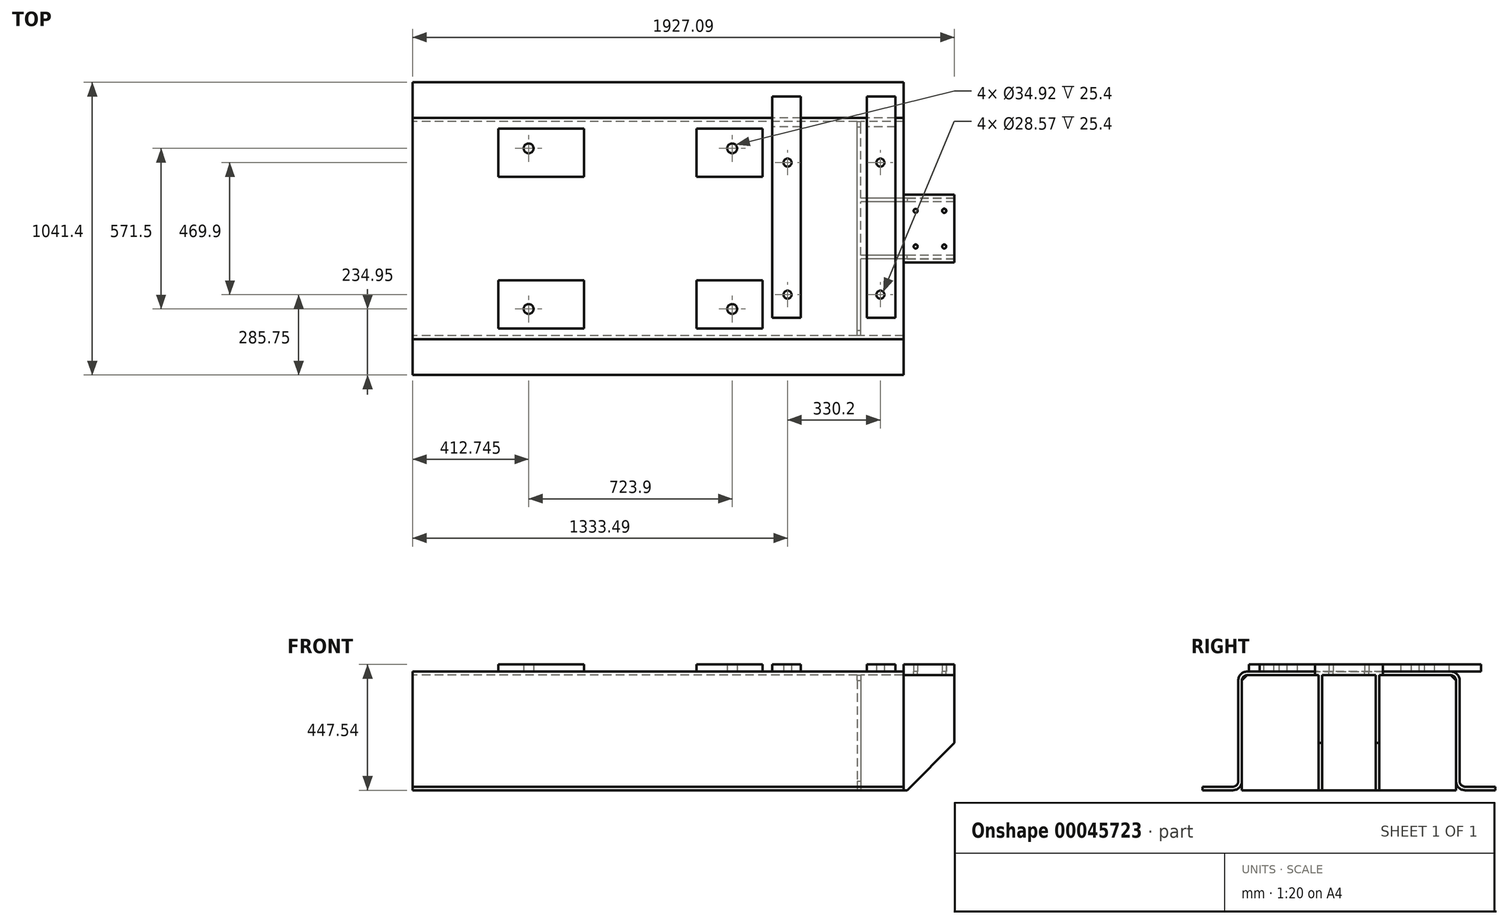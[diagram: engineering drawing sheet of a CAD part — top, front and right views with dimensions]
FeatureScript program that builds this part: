
annotation { "Feature Type Name" : "Feature", "Feature Type Description" : "" }
export const myFeature = defineFeature(function(context is Context, id is Id, definition is map)
    precondition{}
    {
        {
            var Q0;
            Q0=qCreatedBy(makeId("Right.planeOp"),FACE);
            var sketch = newSketch(context, id + "F0", { "sketchPlane" : qUnion([Q0])});
            skLineSegment(sketch, "E0.rect.bottom", {"start": v(-361.95, 211.07) * mm, "end": v(361.95, 211.07) * mm});
            skLineSegment(sketch, "E0.rect.top", {"start": v(-520.7, -211.07) * mm, "end": v(-412.75, -211.07) * mm});
            skLineSegment(sketch, "E0.rect.left", {"start": v(-393.7, 179.32) * mm, "end": v(-393.7, -179.32) * mm});
            skLineSegment(sketch, "E0.rect.right", {"start": v(393.7, 179.32) * mm, "end": v(393.7, -179.32) * mm});
            skPoint(sketch, "E0.rect.middle", {"position": v(0, 0) * mm});
            skLineSegment(sketch, "E1.0", {"start": v(-361.95, 198.37) * mm, "end": v(361.95, 198.37) * mm});
            skLineSegment(sketch, "E1.1", {"start": v(-381, 179.32) * mm, "end": v(-381, -179.32) * mm});
            skLineSegment(sketch, "E1.2", {"start": v(-520.7, -198.37) * mm, "end": v(-412.75, -198.37) * mm});
            skLineSegment(sketch, "E1.3", {"start": v(381, 179.32) * mm, "end": v(381, -179.32) * mm});
            skLineSegment(sketch, "E2.0", {"start": v(-520.7, -198.37) * mm, "end": v(-520.7, -211.07) * mm});
            skLineSegment(sketch, "E3", {"start": v(0, 0) * mm, "end": v(0, 407.59) * mm, "construction": true});
            skPoint(sketch, "E4.orphan", {"position": v(-393.7, -211.07) * mm});
            skLineSegment(sketch, "E5.MirrorCS", {"start": v(520.7, -198.37) * mm, "end": v(520.7, -211.07) * mm});
            skPoint(sketch, "E6.MirrorP", {"position": v(393.7, -211.07) * mm});
            skLineSegment(sketch, "E7.MirrorCS", {"start": v(520.7, -211.07) * mm, "end": v(412.75, -211.07) * mm});
            skLineSegment(sketch, "E8.MirrorCS", {"start": v(520.7, -198.37) * mm, "end": v(412.75, -198.37) * mm});
            skPoint(sketch, "E9.visualSharp", {"position": v(-393.7, -198.37) * mm});
            skArc(sketch, "E9.filletArc", {"start": v(-412.75, -198.37) * mm, "mid": v(-399.28, -192.8) * mm, "end": v(-393.7, -179.32) * mm});
            skPoint(sketch, "E10.visualSharp", {"position": v(-381, 198.37) * mm});
            skArc(sketch, "E10.filletArc", {"start": v(-361.95, 198.37) * mm, "mid": v(-375.42, 192.8) * mm, "end": v(-381, 179.32) * mm});
            skPoint(sketch, "E11.visualSharp", {"position": v(381, 198.37) * mm});
            skArc(sketch, "E11.filletArc", {"start": v(381, 179.32) * mm, "mid": v(375.42, 192.8) * mm, "end": v(361.95, 198.37) * mm});
            skPoint(sketch, "E12.visualSharp", {"position": v(393.7, -198.37) * mm});
            skArc(sketch, "E12.filletArc", {"start": v(393.7, -179.32) * mm, "mid": v(399.28, -192.8) * mm, "end": v(412.75, -198.37) * mm});
            skPoint(sketch, "E13.visualSharp", {"position": v(-381, -211.07) * mm});
            skArc(sketch, "E13.filletArc", {"start": v(-412.75, -211.07) * mm, "mid": v(-390.3, -201.77) * mm, "end": v(-381, -179.32) * mm});
            skPoint(sketch, "E14.visualSharp", {"position": v(-393.7, 211.07) * mm});
            skArc(sketch, "E14.filletArc", {"start": v(-361.95, 211.07) * mm, "mid": v(-384.4, 201.77) * mm, "end": v(-393.7, 179.32) * mm});
            skPoint(sketch, "E15.visualSharp", {"position": v(393.7, 211.07) * mm});
            skArc(sketch, "E15.filletArc", {"start": v(393.7, 179.32) * mm, "mid": v(384.4, 201.77) * mm, "end": v(361.95, 211.07) * mm});
            skPoint(sketch, "E16.visualSharp", {"position": v(381, -211.07) * mm});
            skArc(sketch, "E16.filletArc", {"start": v(381, -179.32) * mm, "mid": v(390.3, -201.77) * mm, "end": v(412.75, -211.07) * mm});
            skSolve(sketch);
        }
        {
            var Q0;
            Q0 = qSketchRegion(id + "F0", true);
            extrude(context, id + "F1", {"entities" : qUnion([Q0]), "endBound" : BoundingType.SYMMETRIC, "depth" : 1746.25 * mm});
        }
        {
            var Q0;
            Q0=makeQuery(id+"F1.opExtrude","CAP_FACE",FACE,{"disambiguationData":[OSD([sQuery(id+"F0.wireOp",EDGE,"E0.rect.bottom"),sQuery(id+"F0.wireOp",EDGE,"E0.rect.top"),sQuery(id+"F0.wireOp",EDGE,"E0.rect.left"),sQuery(id+"F0.wireOp",EDGE,"E0.rect.right"),sQuery(id+"F0.wireOp",EDGE,"E1.0"),sQuery(id+"F0.wireOp",EDGE,"E1.1"),sQuery(id+"F0.wireOp",EDGE,"E1.2"),sQuery(id+"F0.wireOp",EDGE,"E1.3"),sQuery(id+"F0.wireOp",EDGE,"E2.0"),sQuery(id+"F0.wireOp",EDGE,"E5.MirrorCS"),sQuery(id+"F0.wireOp",EDGE,"E7.MirrorCS"),sQuery(id+"F0.wireOp",EDGE,"E8.MirrorCS"),sQuery(id+"F0.wireOp",EDGE,"E9.filletArc"),sQuery(id+"F0.wireOp",EDGE,"E10.filletArc"),sQuery(id+"F0.wireOp",EDGE,"E11.filletArc"),sQuery(id+"F0.wireOp",EDGE,"E12.filletArc"),sQuery(id+"F0.wireOp",EDGE,"E13.filletArc"),sQuery(id+"F0.wireOp",EDGE,"E14.filletArc"),sQuery(id+"F0.wireOp",EDGE,"E15.filletArc"),sQuery(id+"F0.wireOp",EDGE,"E16.filletArc")])],"isStart":false});
            cPlane(context, id + "F2", {"entities" : qUnion([Q0]), "cplaneType" : CPlaneType.OFFSET, "offset" : 152.4 * mm, "oppositeDirection" : true, "width" : 152.4 * mm, "height" : 152.4 * mm});
        }
        {
            var Q0;
            Q0=qCreatedBy(id+"F2.planeOp",FACE);
            var sketch = newSketch(context, id + "F3", { "sketchPlane" : qUnion([Q0])});
            skLineSegment(sketch, "E17.0", {"start": v(-361.95, 198.37) * mm, "end": v(361.95, 198.37) * mm});
            skLineSegment(sketch, "E18.0", {"start": v(-381, 179.32) * mm, "end": v(-381, -211.07) * mm});
            skLineSegment(sketch, "E19.0", {"start": v(381, 179.32) * mm, "end": v(381, -211.07) * mm});
            skLineSegment(sketch, "E20.0", {"start": v(-381, -211.07) * mm, "end": v(381, -211.07) * mm});
            skLineSegment(sketch, "E21", {"start": v(-381, 179.32) * mm, "end": v(-361.95, 198.37) * mm});
            skLineSegment(sketch, "E22", {"start": v(361.95, 198.37) * mm, "end": v(381, 179.32) * mm});
            skPoint(sketch, "E23.orphan", {"position": v(-412.75, -211.07) * mm});
            skPoint(sketch, "E24.orphan", {"position": v(381, -179.32) * mm});
            skPoint(sketch, "E25.orphan", {"position": v(-381, -179.32) * mm});
            skPoint(sketch, "E26.orphan", {"position": v(-520.7, -211.07) * mm});
            skSolve(sketch);
        }
        {
            var Q0;
            Q0 = qSketchRegion(id + "F3", true);
            extrude(context, id + "F4", {"entities" : qUnion([Q0]), "oppositeDirection" : true, "depth" : 12.7 * mm});
        }
        {
            var Q0;
            Q0=makeQuery(id+"F1.opExtrude","SWEPT_FACE",FACE,{"disambiguationData":[OSD([sQuery(id+"F0.wireOp",EDGE,"E0.rect.bottom")])]});
            var sketch = newSketch(context, id + "F5", { "sketchPlane" : qUnion([Q0])});
            skLineSegment(sketch, "E27.0", {"start": v(-98.42, -361.95) * mm, "end": v(-98.42, 361.95) * mm, "construction": true});
            skLineSegment(sketch, "E28.0", {"start": v(136.53, -361.95) * mm, "end": v(136.53, 361.95) * mm, "construction": true});
            skLineSegment(sketch, "E29.0", {"start": v(371.48, -361.95) * mm, "end": v(371.48, 361.95) * mm, "construction": true});
            skLineSegment(sketch, "E30.0", {"start": v(-263.53, -361.95) * mm, "end": v(-263.53, 361.95) * mm, "construction": true});
            skLineSegment(sketch, "E31.0", {"start": v(-568.32, -361.95) * mm, "end": v(-568.32, 361.95) * mm, "construction": true});
            skLineSegment(sketch, "E32", {"start": v(-1011.97, 0) * mm, "end": v(1200.8, 0) * mm, "construction": true});
            skLineSegment(sketch, "E33.0", {"start": v(-1011.97, -184.15) * mm, "end": v(1200.8, -184.15) * mm, "construction": true});
            skLineSegment(sketch, "E34.0", {"start": v(-1011.97, -355.6) * mm, "end": v(1200.8, -355.6) * mm, "construction": true});
            skLineSegment(sketch, "E35.bottom", {"start": v(-568.32, -184.15) * mm, "end": v(-263.53, -184.15) * mm});
            skLineSegment(sketch, "E35.top", {"start": v(-568.32, -355.6) * mm, "end": v(-263.52, -355.6) * mm});
            skLineSegment(sketch, "E35.left", {"start": v(-568.32, -184.15) * mm, "end": v(-568.32, -355.6) * mm});
            skLineSegment(sketch, "E35.right", {"start": v(-263.53, -184.15) * mm, "end": v(-263.53, -355.6) * mm});
            skLineSegment(sketch, "E36.bottom", {"start": v(136.53, -184.15) * mm, "end": v(371.48, -184.15) * mm});
            skLineSegment(sketch, "E36.top", {"start": v(136.53, -355.6) * mm, "end": v(371.48, -355.6) * mm});
            skLineSegment(sketch, "E36.left", {"start": v(136.53, -184.15) * mm, "end": v(136.53, -355.6) * mm});
            skLineSegment(sketch, "E36.right", {"start": v(371.48, -184.15) * mm, "end": v(371.48, -355.6) * mm});
            skLineSegment(sketch, "E37.0", {"start": v(-460.38, -361.95) * mm, "end": v(-460.38, 361.95) * mm, "construction": true});
            skLineSegment(sketch, "E38.0", {"start": v(-1011.97, -285.75) * mm, "end": v(1200.8, -285.75) * mm, "construction": true});
            skCircle(sketch, "E39", {"center": v(-460.38, -285.75) * mm, "radius": 17.46 * mm});
            skCircle(sketch, "E40.MirrorC", {"center": v(263.53, -285.75) * mm, "radius": 17.46 * mm});
            skCircle(sketch, "E41.MirrorC", {"center": v(-460.38, 285.75) * mm, "radius": 17.46 * mm});
            skCircle(sketch, "E42.MirrorC", {"center": v(263.53, 285.75) * mm, "radius": 17.46 * mm});
            skLineSegment(sketch, "E43.MirrorCS", {"start": v(-568.32, 184.15) * mm, "end": v(-263.53, 184.15) * mm});
            skLineSegment(sketch, "E44.MirrorCS", {"start": v(-568.33, 355.6) * mm, "end": v(-263.53, 355.6) * mm});
            skLineSegment(sketch, "E45.MirrorCS", {"start": v(-568.32, 184.15) * mm, "end": v(-568.32, 355.6) * mm});
            skLineSegment(sketch, "E46.MirrorCS", {"start": v(-263.53, 184.15) * mm, "end": v(-263.53, 355.6) * mm});
            skLineSegment(sketch, "E47.MirrorCS", {"start": v(136.53, 184.15) * mm, "end": v(371.48, 184.15) * mm});
            skLineSegment(sketch, "E48.MirrorCS", {"start": v(136.52, 355.6) * mm, "end": v(371.47, 355.6) * mm});
            skLineSegment(sketch, "E49.MirrorCS", {"start": v(371.48, 184.15) * mm, "end": v(371.48, 355.6) * mm});
            skLineSegment(sketch, "E50.MirrorCS", {"start": v(136.53, 184.15) * mm, "end": v(136.52, 355.6) * mm});
            skSolve(sketch);
        }
        {
            var Q0;
            Q0 = qSketchRegion(id + "F5", true);
            extrude(context, id + "F6", {"entities" : qUnion([Q0]), "operationType" : NewBodyOperationType.ADD, "depth" : 25.4 * mm});
        }
        {
            var Q0;
            Q0=makeQuery(id+"F5.imprint","IMPRINT",FACE,{"disambiguationData":[TD([[makeQuery(id+"F5.imprint","IMPRINT",EDGE,{"derivedFrom":sQuery(id+"F5.wireOp",EDGE,"E35.bottom")}),1.0]])]});
            var sketch = newSketch(context, id + "F7", { "sketchPlane" : qUnion([Q0])});
            skLineSegment(sketch, "E51.0", {"start": v(-98.42, -361.95) * mm, "end": v(-98.42, 361.95) * mm, "construction": true});
            skLineSegment(sketch, "E52.0", {"start": v(625.48, -361.95) * mm, "end": v(625.48, 361.95) * mm, "construction": true});
            skLineSegment(sketch, "E53.0", {"start": v(508.13, -317.5) * mm, "end": v(508.13, 469.9) * mm});
            skLineSegment(sketch, "E54.0", {"start": v(406.53, -317.5) * mm, "end": v(406.53, 469.9) * mm});
            skLineSegment(sketch, "E55", {"start": v(0, 0) * mm, "end": v(1304.94, 0) * mm, "construction": true});
            skLineSegment(sketch, "E56.0", {"start": v(406.53, -317.5) * mm, "end": v(508.13, -317.5) * mm});
            skLineSegment(sketch, "E57.0", {"start": v(406.53, 469.9) * mm, "end": v(508.13, 469.9) * mm});
            skLineSegment(sketch, "E58.filletArc", {"start": v(406.53, 469.9) * mm, "end": v(406.53, 469.9) * mm});
            skLineSegment(sketch, "E59.filletArc", {"start": v(508.13, 469.9) * mm, "end": v(508.13, 469.9) * mm});
            skLineSegment(sketch, "E60.filletArc", {"start": v(406.53, -317.5) * mm, "end": v(406.53, -317.5) * mm});
            skLineSegment(sketch, "E61.filletArc", {"start": v(508.13, -317.5) * mm, "end": v(508.13, -317.5) * mm});
            skLineSegment(sketch, "E62.0", {"start": v(0, 234.95) * mm, "end": v(1304.94, 234.95) * mm, "construction": true});
            skLineSegment(sketch, "E63.0", {"start": v(0, -234.95) * mm, "end": v(1304.94, -234.95) * mm, "construction": true});
            skLineSegment(sketch, "E64.0", {"start": v(460.38, -361.95) * mm, "end": v(460.38, 361.95) * mm, "construction": true});
            skCircle(sketch, "E65", {"center": v(460.38, -234.95) * mm, "radius": 14.29 * mm});
            skCircle(sketch, "E66", {"center": v(460.38, 234.95) * mm, "radius": 14.29 * mm});
            skLineSegment(sketch, "E67.MirrorCS", {"start": v(742.82, -317.5) * mm, "end": v(742.82, -317.5) * mm});
            skCircle(sketch, "E68.MirrorC", {"center": v(790.58, -234.95) * mm, "radius": 14.29 * mm});
            skCircle(sketch, "E69.MirrorC", {"center": v(790.58, 234.95) * mm, "radius": 14.29 * mm});
            skLineSegment(sketch, "E70.MirrorCS", {"start": v(742.82, 469.9) * mm, "end": v(742.82, 469.9) * mm});
            skLineSegment(sketch, "E71.MirrorCS", {"start": v(844.42, 469.9) * mm, "end": v(844.42, 469.9) * mm});
            skLineSegment(sketch, "E72.MirrorCS", {"start": v(742.82, -317.5) * mm, "end": v(742.82, 469.9) * mm});
            skLineSegment(sketch, "E73.MirrorCS", {"start": v(844.42, -317.5) * mm, "end": v(844.42, 469.9) * mm});
            skLineSegment(sketch, "E74.MirrorCS", {"start": v(844.42, -317.5) * mm, "end": v(742.82, -317.5) * mm});
            skLineSegment(sketch, "E75.MirrorCS", {"start": v(844.42, 469.9) * mm, "end": v(742.82, 469.9) * mm});
            skLineSegment(sketch, "E76.MirrorCS", {"start": v(844.42, -317.5) * mm, "end": v(844.42, -317.5) * mm});
            skSolve(sketch);
        }
        {
            var Q0;
            Q0 = qSketchRegion(id + "F7", true);
            extrude(context, id + "F8", {"entities" : qUnion([Q0]), "operationType" : NewBodyOperationType.ADD, "depth" : 25.4 * mm});
        }
        {
            var Q0;
            {var subQ0=sQuery(id+"F0.wireOp",EDGE,"E0.rect.bottom");var subQ32=sQuery(id+"F0.wireOp",EDGE,"E14.filletArc");var subQ35=makeQuery(id+"F1.opExtrude","SWEPT_FACE",FACE,{"disambiguationData":[OSD([subQ32])]});Q0=makeQuery(id+"F8.boolean.opBoolean","SPLIT",FACE,{"disambiguationData":[TD([subQ35])],"derivedFrom":makeQuery(id+"F6.boolean.opBoolean","SPLIT",FACE,{"disambiguationData":[TD([subQ35])],"derivedFrom":makeQuery(id+"F1.opExtrude","SWEPT_FACE",FACE,{"disambiguationData":[OSD([subQ0])]})})});}
            var sketch = newSketch(context, id + "F9", { "sketchPlane" : qUnion([Q0])});
            skLineSegment(sketch, "E77.0.0", {"start": v(742.82, 469.9) * mm, "end": v(742.82, -317.5) * mm, "construction": true});
            skLineSegment(sketch, "E77.0.1", {"start": v(742.82, -317.5) * mm, "end": v(844.42, -317.5) * mm, "construction": true});
            skLineSegment(sketch, "E77.0.2", {"start": v(844.42, -317.5) * mm, "end": v(844.42, 469.9) * mm, "construction": true});
            skLineSegment(sketch, "E77.0.3", {"start": v(844.42, 469.9) * mm, "end": v(742.82, 469.9) * mm, "construction": true});
            skLineSegment(sketch, "E78.0", {"start": v(1053.97, 469.9) * mm, "end": v(1053.97, -317.5) * mm, "construction": true});
            skLineSegment(sketch, "E79", {"start": v(0, 0) * mm, "end": v(1391.66, 0) * mm, "construction": true});
            skLineSegment(sketch, "E80.0", {"start": v(0, 120.65) * mm, "end": v(1391.66, 120.65) * mm});
            skLineSegment(sketch, "E81.0", {"start": v(708.02, -361.95) * mm, "end": v(708.02, 361.95) * mm, "construction": true});
            skLineSegment(sketch, "E82.0", {"start": v(720.73, -361.95) * mm, "end": v(720.73, 361.95) * mm, "construction": true});
            skLineSegment(sketch, "E83.0", {"start": v(873.12, -361.95) * mm, "end": v(873.12, 361.95) * mm, "construction": true});
            skLineSegment(sketch, "E84.bottom", {"start": v(873.12, 120.65) * mm, "end": v(1053.97, 120.65) * mm});
            skLineSegment(sketch, "E84.top", {"start": v(873.12, -120.65) * mm, "end": v(1053.97, -120.65) * mm});
            skLineSegment(sketch, "E84.left", {"start": v(873.12, 120.65) * mm, "end": v(873.12, -120.65) * mm});
            skLineSegment(sketch, "E84.right", {"start": v(1053.97, 120.65) * mm, "end": v(1053.97, -120.65) * mm});
            skSolve(sketch);
        }
        {
            var Q0;
            Q0 = qSketchRegion(id + "F9", true);
            extrude(context, id + "F10", {"entities" : qUnion([Q0]), "operationType" : NewBodyOperationType.ADD, "oppositeDirection" : true, "depth" : 12.7 * mm});
        }
        {
            var Q0;
            Q0=qCreatedBy(makeId("Front.planeOp"),FACE);
            cPlane(context, id + "F11", {"entities" : qUnion([Q0]), "cplaneType" : CPlaneType.OFFSET, "offset" : 95.25 * mm, "oppositeDirection" : true, "width" : 152.4 * mm, "height" : 152.4 * mm});
        }
        {
            var Q0;
            Q0=qCreatedBy(id+"F11.planeOp",FACE);
            var sketch = newSketch(context, id + "F12", { "sketchPlane" : qUnion([Q0])});
            skLineSegment(sketch, "E85.0", {"start": v(873.12, 198.37) * mm, "end": v(1053.97, 198.37) * mm, "construction": true});
            skPoint(sketch, "E86.0", {"position": v(720.73, 179.32) * mm});
            skLineSegment(sketch, "E87", {"start": v(720.73, 179.32) * mm, "end": v(720.73, -266.28) * mm, "construction": true});
            skLineSegment(sketch, "E88.0", {"start": v(873.12, -211.07) * mm, "end": v(-873.12, -211.07) * mm, "construction": true});
            skLineSegment(sketch, "E89.bottom", {"start": v(1053.97, 198.37) * mm, "end": v(720.73, 198.37) * mm});
            skLineSegment(sketch, "E89.top", {"start": v(1053.97, -211.07) * mm, "end": v(720.73, -211.07) * mm});
            skLineSegment(sketch, "E89.left", {"start": v(1053.97, 198.37) * mm, "end": v(1053.97, -211.07) * mm});
            skLineSegment(sketch, "E89.right", {"start": v(720.73, 198.37) * mm, "end": v(720.73, -211.07) * mm});
            skSolve(sketch);
        }
        {
            var Q0;
            Q0 = qSketchRegion(id + "F12", true);
            extrude(context, id + "F13", {"entities" : qUnion([Q0]), "oppositeDirection" : true, "depth" : 12.7 * mm});
        }
        {
            var Q0;
            Q0=makeQuery(id+"F13.opExtrude","SWEPT_EDGE",EDGE,{"disambiguationData":[OSD([sQuery(id+"F12.wireOp",EDGE,"E89.top"),sQuery(id+"F12.wireOp",EDGE,"E89.left")])]});
            chamfer(context, id + "F14", {"entities" : qUnion([Q0]), "width" : 168.15 * mm, "tangentPropagation" : true});
        }
        {
            var Q0;
            Q0=makeQuery(id+"F13.opExtrude","SWEPT_BODY",BODY,{"disambiguationData":[OSD([sQuery(id+"F12.wireOp",EDGE,"E89.bottom"),sQuery(id+"F12.wireOp",EDGE,"E89.top"),sQuery(id+"F12.wireOp",EDGE,"E89.left"),sQuery(id+"F12.wireOp",EDGE,"E89.right")])]});
            var Q1;
            Q1=qCreatedBy(makeId("Front.planeOp"),FACE);
            mirror(context, id + "F15", {"operationType" : NewBodyOperationType.ADD, "entities" : qUnion([Q0]), "mirrorPlane" : qUnion([Q1])});
        }
        {
            var Q0;
            {var subQ0=sQuery(id+"F0.wireOp",EDGE,"E0.rect.bottom");var subQ32=sQuery(id+"F0.wireOp",EDGE,"E14.filletArc");var subQ35=makeQuery(id+"F1.opExtrude","SWEPT_FACE",FACE,{"disambiguationData":[OSD([subQ32])]});Q0=makeQuery(id+"F10.boolean.opBoolean","MERGE",FACE,{"derivedFrom":[makeQuery(id+"F8.boolean.opBoolean","SPLIT",FACE,{"disambiguationData":[TD([subQ35])],"derivedFrom":makeQuery(id+"F6.boolean.opBoolean","SPLIT",FACE,{"disambiguationData":[TD([subQ35])],"derivedFrom":makeQuery(id+"F1.opExtrude","SWEPT_FACE",FACE,{"disambiguationData":[OSD([subQ0])]})})}),makeQuery(id+"F10.opExtrude","CAP_FACE",FACE,{"disambiguationData":[OSD([sQuery(id+"F9.wireOp",EDGE,"E84.bottom"),sQuery(id+"F9.wireOp",EDGE,"E84.top"),sQuery(id+"F9.wireOp",EDGE,"E84.left"),sQuery(id+"F9.wireOp",EDGE,"E84.right")])],"isStart":true})]});}
            var sketch = newSketch(context, id + "F16", { "sketchPlane" : qUnion([Q0])});
            skLineSegment(sketch, "E90", {"start": v(0, 0) * mm, "end": v(1237.02, 0) * mm, "construction": true});
            skLineSegment(sketch, "E91.0", {"start": v(625.48, -361.95) * mm, "end": v(625.48, 361.95) * mm, "construction": true});
            skLineSegment(sketch, "E92.0", {"start": v(916.05, -361.95) * mm, "end": v(916.05, 361.95) * mm, "construction": true});
            skLineSegment(sketch, "E93.0", {"start": v(1017.65, -361.95) * mm, "end": v(1017.65, 361.95) * mm, "construction": true});
            skLineSegment(sketch, "E94.0", {"start": v(0, -63.5) * mm, "end": v(1237.02, -63.5) * mm, "construction": true});
            skLineSegment(sketch, "E95.0", {"start": v(0, 63.5) * mm, "end": v(1237.02, 63.5) * mm, "construction": true});
            skCircle(sketch, "E96", {"center": v(916.05, 63.5) * mm, "radius": 7.14 * mm});
            skCircle(sketch, "E97", {"center": v(1017.65, 63.5) * mm, "radius": 7.14 * mm});
            skCircle(sketch, "E98", {"center": v(1017.65, -63.5) * mm, "radius": 7.14 * mm});
            skCircle(sketch, "E99", {"center": v(916.05, -63.5) * mm, "radius": 7.14 * mm});
            skSolve(sketch);
        }
        {
            var Q0;
            Q0 = qSketchRegion(id + "F16", true);
            extrude(context, id + "F17", {"entities" : qUnion([Q0]), "operationType" : NewBodyOperationType.REMOVE, "endBound" : BoundingType.THROUGH_ALL, "oppositeDirection" : true, "depth" : 25.4 * mm});
        }
        {
            var Q0;
            {var subQ0=sQuery(id+"F0.wireOp",EDGE,"E0.rect.bottom");var subQ32=sQuery(id+"F0.wireOp",EDGE,"E14.filletArc");var subQ35=makeQuery(id+"F1.opExtrude","SWEPT_FACE",FACE,{"disambiguationData":[OSD([subQ32])]});Q0=makeQuery(id+"F10.boolean.opBoolean","MERGE",FACE,{"derivedFrom":[makeQuery(id+"F8.boolean.opBoolean","SPLIT",FACE,{"disambiguationData":[TD([subQ35])],"derivedFrom":makeQuery(id+"F6.boolean.opBoolean","SPLIT",FACE,{"disambiguationData":[TD([subQ35])],"derivedFrom":makeQuery(id+"F1.opExtrude","SWEPT_FACE",FACE,{"disambiguationData":[OSD([subQ0])]})})}),makeQuery(id+"F10.opExtrude","CAP_FACE",FACE,{"disambiguationData":[OSD([sQuery(id+"F9.wireOp",EDGE,"E84.bottom"),sQuery(id+"F9.wireOp",EDGE,"E84.top"),sQuery(id+"F9.wireOp",EDGE,"E84.left"),sQuery(id+"F9.wireOp",EDGE,"E84.right")])],"isStart":true})]});}
            var sketch = newSketch(context, id + "F18", { "sketchPlane" : qUnion([Q0])});
            skLineSegment(sketch, "E100.bottom", {"start": v(1053.97, 120.65) * mm, "end": v(873.12, 120.65) * mm});
            skLineSegment(sketch, "E100.top", {"start": v(1053.97, -120.65) * mm, "end": v(873.12, -120.65) * mm});
            skLineSegment(sketch, "E100.left", {"start": v(1053.97, 120.65) * mm, "end": v(1053.97, -120.65) * mm});
            skLineSegment(sketch, "E100.right", {"start": v(873.12, 120.65) * mm, "end": v(873.12, -120.65) * mm});
            skCircle(sketch, "E101", {"center": v(916.05, 63.5) * mm, "radius": 7.13 * mm});
            skCircle(sketch, "E102", {"center": v(1017.65, 63.5) * mm, "radius": 7.46 * mm});
            skCircle(sketch, "E103", {"center": v(916.05, -63.5) * mm, "radius": 7.32 * mm});
            skCircle(sketch, "E104", {"center": v(1017.65, -63.5) * mm, "radius": 7.25 * mm});
            skSolve(sketch);
        }
        {
            var Q0;
            Q0 = qSketchRegion(id + "F18", true);
            extrude(context, id + "F19", {"entities" : qUnion([Q0]), "operationType" : NewBodyOperationType.ADD, "depth" : 25.4 * mm});
        }
    });
